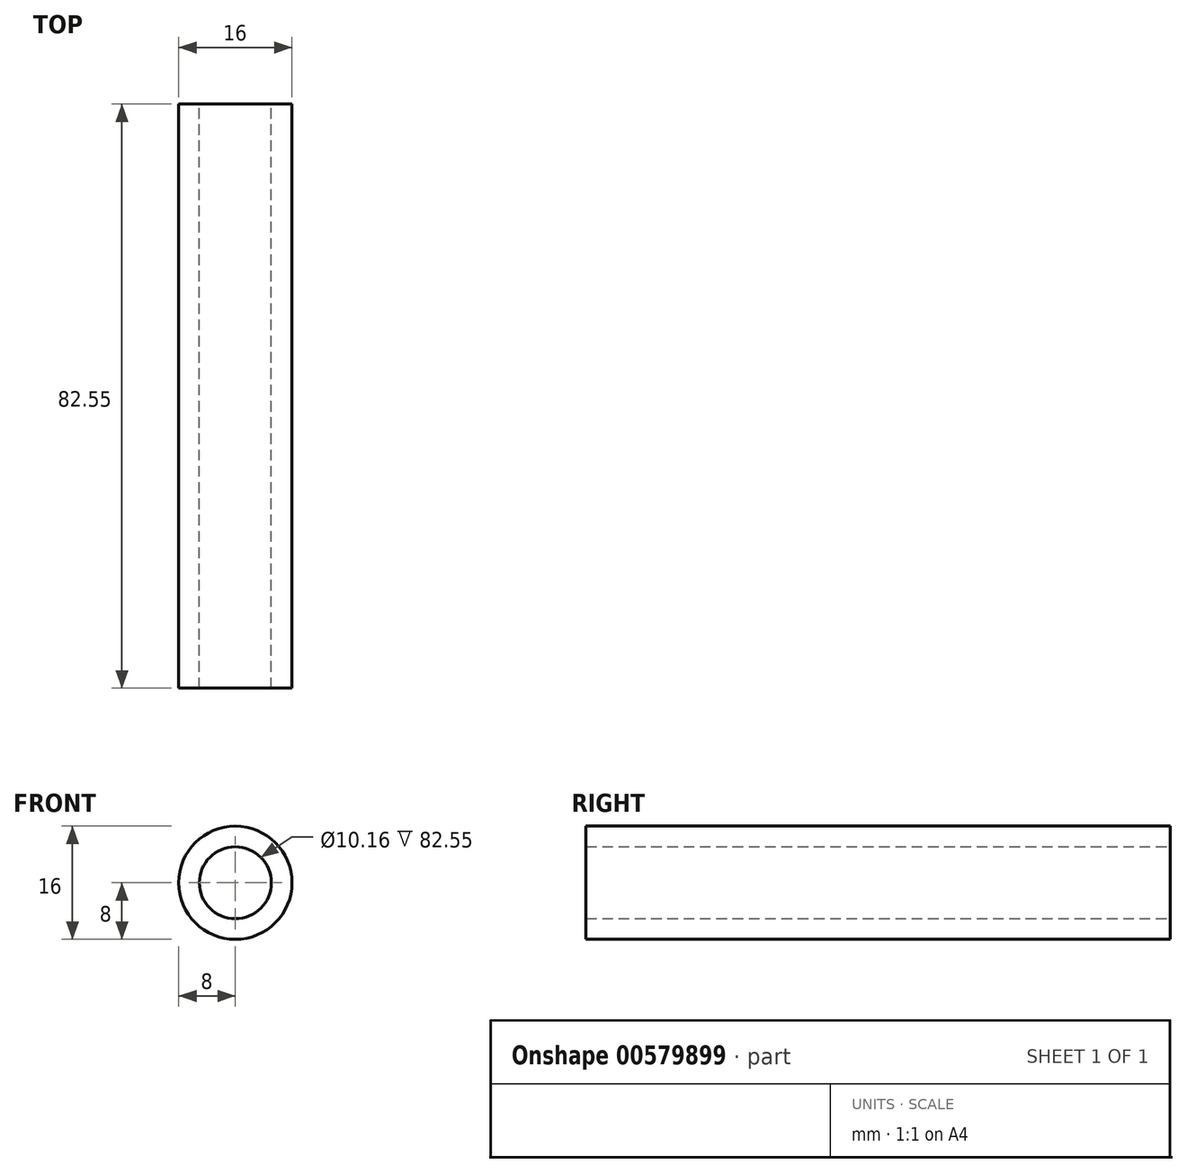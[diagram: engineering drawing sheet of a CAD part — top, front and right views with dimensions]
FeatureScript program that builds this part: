
annotation { "Feature Type Name" : "Feature", "Feature Type Description" : "" }
export const myFeature = defineFeature(function(context is Context, id is Id, definition is map)
    precondition{}
    {
        {
            var Q0;
            Q0=qCreatedBy(makeId("Front.planeOp"),FACE);
            var sketch = newSketch(context, id + "F0", { "sketchPlane" : qUnion([Q0])});
            skCircle(sketch, "E0", {"center": v(0, 0) * mm, "radius": 8 * mm});
            skCircle(sketch, "E1", {"center": v(0, 0) * mm, "radius": 5.08 * mm});
            skSolve(sketch);
        }
        {
            var Q0;
            Q0 = qSketchRegion(id + "F0", true);
            extrude(context, id + "F1", {"entities" : qUnion([Q0]), "depth" : 82.55 * mm, "offsetDistance" : 25.4 * mm});
        }
    });
